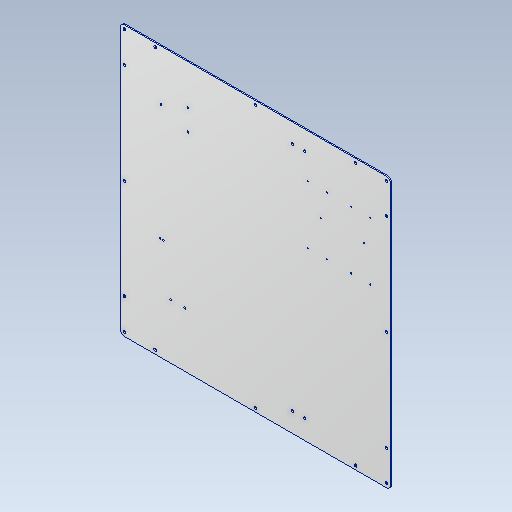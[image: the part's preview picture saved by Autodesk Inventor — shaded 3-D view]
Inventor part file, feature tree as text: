
AUTODESK INVENTOR PART (.ipt)
format: ipt  version: 2020 (Build 240168000, 168)  size: 227,328 bytes
history: native  units: mm
features: reference x19, other x13, sketch x3, extrude x2, hole x1, fillet x1
ambient origin geometry x8: Origin, YZ Plane, XZ Plane, XY Plane, X Axis, Y Axis, Z Axis, Center Point
bodies: Solid1 (feature_tree)
feature tree (39):
  extrude  "Extrusion1"  Depth=700.0mm
  hole  "Hole1"  [1 undecoded]
  extrude  "Extrusion2"  Depth=3.0mm
  fillet  "Fillet1"  Radius=113.333333mm
  sketch  "Sketch1"  dims[d0=700.0mm d1=700.0mm]
  sketch  "Sketch2"  dims[d2=3.0mm d3=0.0mm d4=10.0mm]
  sketch  "Sketch3"  dims[d5=10.0mm d6=340.0mm d7=113.333333mm d8=80.0mm d9=80.0mm d10=80.0mm d11=80.0mm d12=80.0mm d13=80.0mm d14=80.0mm d15=80.0mm d16=80.0mm d17=7.0mm d18=6.0mm d19=4.0mm d20=2.0mm d21=90.0deg d22=8.0mm d23=20.594885mm d24=0.0mm d25=0.0mm d26=10.0mm d27=4.0mm d28=4.0mm d29=8.0mm d30=3.0mm d31=3.0mm d32=16.5mm d33=65.0mm d34=114.0mm d35=150.0mm d36=51.5mm d37=50.0mm d38=16.5mm d39=65.0mm d40=63.0mm d41=114.0mm d42=150.0mm d43=50.0mm]
  reference  "Reference1"
  reference  "Reference2"
  reference  "Reference3"
  reference  "Reference4"
  reference  "Reference9"
  reference  "Reference15"
  reference  "Reference17"
  reference  "Reference18"
  reference  "Reference19"
  reference  "Reference20"
  reference  "Reference21"
  reference  "Reference22"
  reference  "Reference23"
  reference  "Reference24"
  reference  "Reference25"
  reference  "Reference26"
  reference  "Reference27"
  reference  "Reference28"
  reference  "Reference29"
  other  "<path> 2.1 Aracet.iam"
  other  "I.A.B 2.1 Aracet.iam"
  other  "0008-10-1022 SHF10:1"
  other  "0008-10-1022 SHF10:2"
  other  "00008-20-1004 PowerSupplyLedMax500:1"
  other  "00008-20-1004 PowerSupplyLedMax500:2"
  other  "0008-10-049 Capac Mofset:1"
  other  "0008-10-027 Cutie Arduino:1"
  other  "<path> 2.1 Aracet_Subansamble.iam"
  other  "I.A.B 2.1 Aracet_Subansamble.iam"
  other  "0008-10-03 YAxis.iam:4"
  other  "0008-10-1026 wire chain Y.ipt:43"
  other  "0008-10-028 Cutie Elemente incalzire.ipt:6"
note: 1 required parameter value undecoded (feature->parameter linkage not recoverable at this tier; creation-order binding heuristic only, values carry confidence <= 0.55)
note: 2 file-system paths scrubbed to <path> (originals preserved in map.json)
